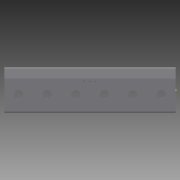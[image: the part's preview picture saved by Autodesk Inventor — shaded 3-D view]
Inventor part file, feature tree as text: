
AUTODESK INVENTOR PART (.ipt)
format: ipt  version: 2015 (Build 190159000, 159)  size: 352,768 bytes
history: native  units: mm
features: hole x21, sketch x7, other x7, sheet_metal_op x3
ambient origin geometry x8: Origin, YZ Plane, XZ Plane, XY Plane, X Axis, Y Axis, Z Axis, Center Point
bodies: Solid1 (feature_tree)
feature tree (38):
  sheet_metal_op  "Contour Flange1"
  sketch  "Sketch7"  dims[d20=0.5mm d21=6.0mm d22=1.5mm d23=1.5mm d24=1.5mm d25=0.0mm d26=1.5mm d27=0.0mm d28=1.5mm d29=0.0mm d30=1.5mm d31=0.0mm d32=17.0mm d33=8.0mm d34=2.5mm d35=6.0mm d36=4.0mm d37=2.0mm d38=90.0deg d39=4.2mm d40=20.594885mm d41=17.0mm d42=8.0mm d43=2.5mm d44=6.0mm d45=4.0mm d46=2.0mm d47=90.0deg d48=4.2mm d49=20.594885mm d50=17.0mm d51=8.0mm d52=2.5mm d53=6.0mm d54=4.0mm d55=2.0mm d56=90.0deg d57=4.2mm d58=20.594885mm d59=17.0mm d60=8.0mm d61=2.5mm d62=6.0mm d63=4.0mm d64=2.0mm d65=90.0deg d66=4.2mm d67=20.594885mm d68=150.0mm d69=8.0mm d70=2.5mm d71=6.0mm d72=4.0mm d73=2.0mm d74=90.0deg d75=4.2mm d76=20.594885mm d77=150.0mm d78=8.0mm d79=2.5mm d80=6.0mm d81=4.0mm d82=2.0mm d83=90.0deg d84=4.2mm d85=20.594885mm d86=30.0mm d87=25.0mm d88=16.0mm d89=6.0mm d90=4.0mm d91=2.0mm d92=90.0deg d93=1.5mm d94=20.594885mm d95=30.0mm d96=75.0mm d97=16.0mm d98=6.0mm d99=4.0mm d100=2.0mm d101=90.0deg d102=1.5mm d103=20.594885mm d104=30.0mm d105=125.0mm d106=16.0mm d107=6.0mm d108=4.0mm d109=2.0mm d110=90.0deg d111=1.5mm d112=20.594885mm d113=30.0mm d114=25.0mm d115=16.0mm d116=6.0mm d117=4.0mm d118=2.0mm d119=90.0deg d120=1.5mm d121=20.594885mm d122=30.0mm d123=75.0mm d124=16.0mm d125=6.0mm d126=4.0mm d127=2.0mm d128=90.0deg d129=1.5mm d130=20.594885mm d131=25.0mm d132=10.0mm d133=3.0mm d134=6.0mm d135=4.0mm d136=2.0mm d137=90.0deg d138=1.5mm d139=20.594885mm d140=10.0mm d141=75.0mm d142=3.0mm d143=6.0mm d144=4.0mm d145=2.0mm d146=90.0deg d147=1.5mm d148=20.594885mm d149=10.0mm d150=125.0mm d151=3.0mm d152=6.0mm d153=4.0mm d154=2.0mm d155=90.0deg d156=1.5mm d157=20.594885mm d158=10.0mm d159=75.0mm d160=3.0mm d161=6.0mm d162=4.0mm d163=2.0mm d164=90.0deg d165=1.5mm d166=20.594885mm d167=10.0mm d168=25.0mm d169=3.0mm d170=6.0mm d171=4.0mm d172=2.0mm d173=90.0deg d174=1.5mm d175=20.594885mm d190=140.0mm d191=5.0mm d192=3.0mm d193=6.0mm d194=4.0mm d195=2.0mm d196=90.0deg d197=1.5mm d198=20.594885mm d199=150.0mm d200=5.0mm d201=3.0mm d202=6.0mm d203=4.0mm d204=2.0mm d205=90.0deg d206=1.5mm d207=20.594885mm d208=140.0mm d209=5.0mm d210=3.0mm d211=6.0mm d212=4.0mm d213=2.0mm d214=90.0deg d215=1.5mm d216=20.594885mm d226=30.0mm d227=125.0mm d228=16.0mm d229=6.0mm d230=4.0mm d231=2.0mm d232=90.0deg d233=1.5mm d234=20.594885mm d235=125.0mm d236=10.0mm d237=3.0mm d238=6.0mm d239=4.0mm d240=2.0mm d241=90.0deg d242=1.5mm d243=20.594885mm d0=1.5mm d1=0.0mm d2=1.5mm d3=0.0mm d4=1.5mm d5=0.0mm d6=1.5mm d7=0.0mm d178=1.0mm d179=1.0mm]
  other  "A-Side Definition"
  hole  "Hole1"  [1 undecoded]
  hole  "Hole2"  [1 undecoded]
  hole  "Hole3"  [1 undecoded]
  hole  "Hole4"  [1 undecoded]
  hole  "Hole5"  [1 undecoded]
  hole  "Hole6"  [1 undecoded]
  hole  "Hole7"  [1 undecoded]
  hole  "Hole8"  [1 undecoded]
  hole  "Hole9"  [1 undecoded]
  hole  "Hole10"  [1 undecoded]
  hole  "Hole11"  [1 undecoded]
  hole  "Hole12"  [1 undecoded]
  hole  "Hole13"  [1 undecoded]
  hole  "Hole14"  [1 undecoded]
  hole  "Hole15"  [1 undecoded]
  hole  "Hole16"  [1 undecoded]
  hole  "Hole18"  [1 undecoded]
  hole  "Hole19"  [1 undecoded]
  hole  "Hole20"  [1 undecoded]
  hole  "Hole22"  [1 undecoded]
  hole  "Hole23"  [1 undecoded]
  sketch  "Sketch1"  dims[d8=25.0mm d9=35.0mm]
  other  "Plate1"
  sheet_metal_op  "Bend1"
  sheet_metal_op  "Corner1"
  sketch  "Sketch3"  dims[d12=20.0mm d13=20.0mm]
  sketch  "Sketch4"  dims[d14=1.5mm d15=0.75mm]
  sketch  "Sketch5"  dims[d16=3.0mm d17=1.5mm]
  sketch  "Sketch6"  dims[d18=300.0mm d19=1.5mm]
  other  "Cut1"
  other  "Cut2"
  other  "Cut3"
  other  "Cut4"
  other  "Definition1"
  sketch  "Sketch2"  dims[d10=20.0mm d11=10.0mm]
note: 21 required parameter values undecoded (feature->parameter linkage not recoverable at this tier; creation-order binding heuristic only, values carry confidence <= 0.55)
